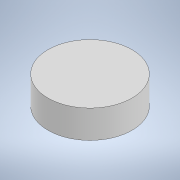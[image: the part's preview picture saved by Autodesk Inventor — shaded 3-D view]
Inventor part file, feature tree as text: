
AUTODESK INVENTOR PART (.ipt)
format: ipt  version: 2021 (Build 250183000, 183)  size: 90,112 bytes
history: native  units: in
note: dims shown in document units (in); Inventor stores cm internally (conversion verified against a paired STEP export)
features: extrude x1, sketch x1
ambient origin geometry x8: Origin, YZ Plane, XZ Plane, XY Plane, X Axis, Y Axis, Z Axis, Center Point
bodies: Solid1 (feature_tree)
feature tree (2):
  extrude  "Extrusion1"  Depth=1.0in TaperAngle=0.0deg
  sketch  "Sketch1"  dims[d0=3.0in d1=1.0in d2=0.0in]
